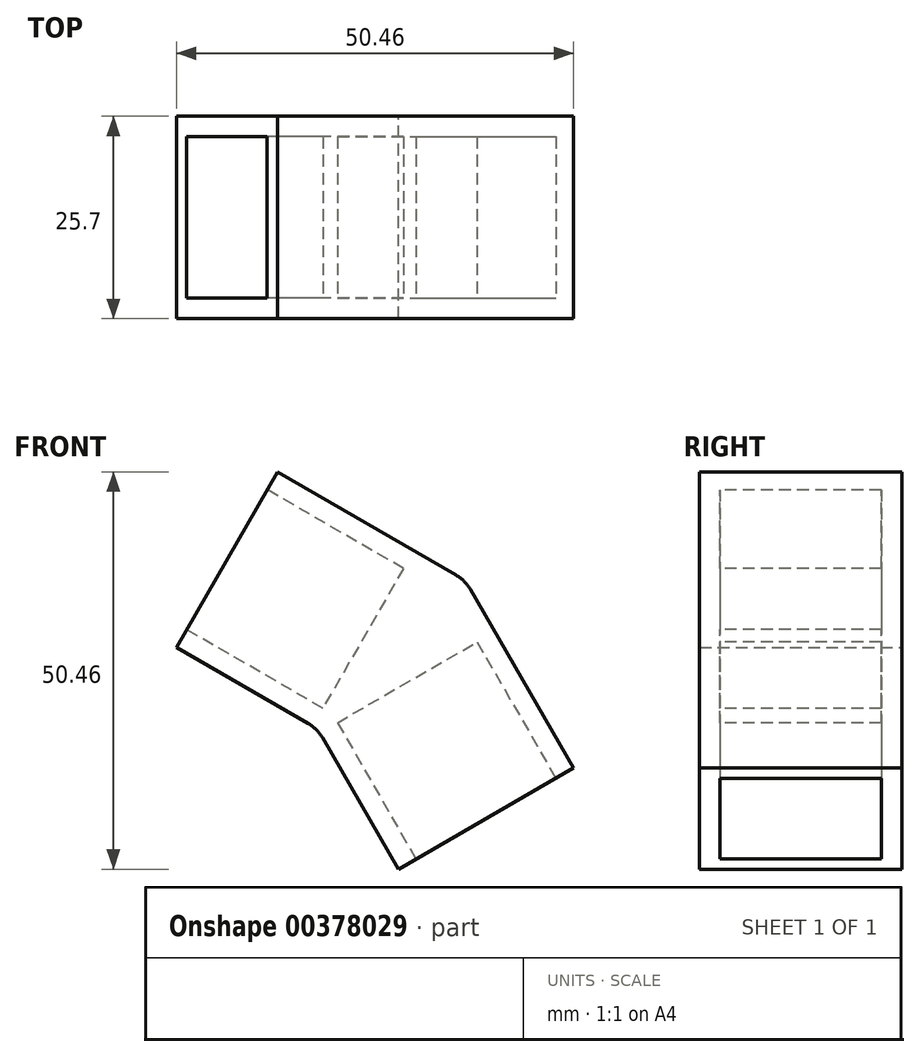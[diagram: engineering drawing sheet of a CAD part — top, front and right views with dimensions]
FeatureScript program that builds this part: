
annotation { "Feature Type Name" : "Feature", "Feature Type Description" : "" }
export const myFeature = defineFeature(function(context is Context, id is Id, definition is map)
    precondition{}
    {
        {
            var Q0;
            Q0=qCreatedBy(makeId("Front.planeOp"),FACE);
            var sketch = newSketch(context, id + "F0", { "sketchPlane" : qUnion([Q0])});
            skLineSegment(sketch, "E0", {"start": v(10.32, -17.88) * mm, "end": v(0.67, -1.16) * mm});
            skLineSegment(sketch, "E1", {"start": v(-1.16, 0.67) * mm, "end": v(-17.88, 10.32) * mm});
            skLineSegment(sketch, "E2", {"start": v(-17.88, 10.32) * mm, "end": v(-5.03, 32.58) * mm});
            skLineSegment(sketch, "E3", {"start": v(-5.03, 32.58) * mm, "end": v(17.65, 19.48) * mm});
            skLineSegment(sketch, "E4", {"start": v(19.48, 17.65) * mm, "end": v(32.58, -5.03) * mm});
            skLineSegment(sketch, "E5", {"start": v(32.58, -5.03) * mm, "end": v(10.32, -17.88) * mm});
            skLineSegment(sketch, "E6", {"start": v(-16.58, 12.58) * mm, "end": v(0.74, 2.58) * mm, "construction": true});
            skLineSegment(sketch, "E7", {"start": v(0.74, 2.58) * mm, "end": v(10.99, 20.33) * mm, "construction": true});
            skLineSegment(sketch, "E8", {"start": v(10.99, 20.33) * mm, "end": v(-6.33, 30.33) * mm, "construction": true});
            skLineSegment(sketch, "E9", {"start": v(12.58, -16.58) * mm, "end": v(2.58, 0.74) * mm, "construction": true});
            skLineSegment(sketch, "E10", {"start": v(2.58, 0.74) * mm, "end": v(20.33, 10.99) * mm, "construction": true});
            skLineSegment(sketch, "E11", {"start": v(20.33, 10.99) * mm, "end": v(30.33, -6.33) * mm, "construction": true});
            skPoint(sketch, "E12.visualSharp", {"position": v(0, 0) * mm});
            skArc(sketch, "E12.filletArc", {"start": v(0.67, -1.16) * mm, "mid": v(-0.12, -0.12) * mm, "end": v(-1.16, 0.67) * mm});
            skPoint(sketch, "E13.visualSharp", {"position": v(18.81, 18.81) * mm});
            skArc(sketch, "E13.filletArc", {"start": v(19.48, 17.65) * mm, "mid": v(18.69, 18.69) * mm, "end": v(17.65, 19.48) * mm});
            skLineSegment(sketch, "E14", {"start": v(0.74, 2.58) * mm, "end": v(0, 2.58) * mm, "construction": true});
            skLineSegment(sketch, "E15", {"start": v(2.58, 0.74) * mm, "end": v(2.58, 0) * mm, "construction": true});
            skSolve(sketch);
        }
        {
            var Q0;
            Q0 = qSketchRegion(id + "F0", true);
            extrude(context, id + "F1", {"entities" : qUnion([Q0]), "depth" : 25.7 * mm});
        }
        {
            var Q0;
            Q0=makeQuery(id+"F1.opExtrude","SWEPT_FACE",FACE,{"disambiguationData":[OSD([sQuery(id+"F0.wireOp",EDGE,"E2")])]});
            var sketch = newSketch(context, id + "F2", { "sketchPlane" : qUnion([Q0])});
            skLineSegment(sketch, "E16.bottom", {"start": v(2.6, 23.1) * mm, "end": v(23.1, 23.1) * mm});
            skLineSegment(sketch, "E16.top", {"start": v(2.6, 2.6) * mm, "end": v(23.1, 2.6) * mm});
            skLineSegment(sketch, "E16.left", {"start": v(2.6, 23.1) * mm, "end": v(2.6, 2.6) * mm});
            skLineSegment(sketch, "E16.right", {"start": v(23.1, 23.1) * mm, "end": v(23.1, 2.6) * mm});
            skSolve(sketch);
        }
        {
            var Q0;
            Q0 = qSketchRegion(id + "F2", true);
            extrude(context, id + "F3", {"entities" : qUnion([Q0]), "operationType" : NewBodyOperationType.REMOVE, "oppositeDirection" : true, "depth" : 20 * mm});
        }
        {
            var Q0;
            Q0=makeQuery(id+"F1.opExtrude","SWEPT_FACE",FACE,{"disambiguationData":[OSD([sQuery(id+"F0.wireOp",EDGE,"E5")])]});
            var sketch = newSketch(context, id + "F4", { "sketchPlane" : qUnion([Q0])});
            skLineSegment(sketch, "E17.bottom", {"start": v(2.6, 2.6) * mm, "end": v(23.1, 2.6) * mm});
            skLineSegment(sketch, "E17.top", {"start": v(2.6, 23.1) * mm, "end": v(23.1, 23.1) * mm});
            skLineSegment(sketch, "E17.left", {"start": v(2.6, 2.6) * mm, "end": v(2.6, 23.1) * mm});
            skLineSegment(sketch, "E17.right", {"start": v(23.1, 2.6) * mm, "end": v(23.1, 23.1) * mm});
            skSolve(sketch);
        }
        {
            var Q0;
            Q0 = qSketchRegion(id + "F4", true);
            extrude(context, id + "F5", {"entities" : qUnion([Q0]), "operationType" : NewBodyOperationType.REMOVE, "oppositeDirection" : true, "depth" : 20 * mm});
        }
    });
